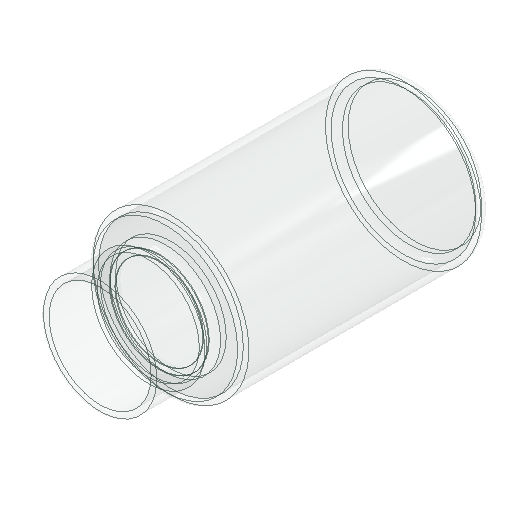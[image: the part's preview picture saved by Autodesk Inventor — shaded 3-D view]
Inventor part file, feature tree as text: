
AUTODESK INVENTOR PART (.ipt)
format: ipt  version: 2024 (Build 280153000, 153)  size: 227,840 bytes
history: native  units: mm
features: fillet x3, revolve x1, shell x1, sketch x1
ambient origin geometry x8: Origin, YZ Plane, XZ Plane, XY Plane, X Axis, Y Axis, Z Axis, Center Point
bodies: Volumenkörper1 (feature_tree)
feature tree (6):
  revolve  "Umdrehung1"
  fillet  "Rundung1"  Radius=13.75mm
  fillet  "Rundung2"  Radius=2.0mm
  shell  "Wandung1"  Thickness=5.0mm
  fillet  "Rundung4"  Radius=56.0mm
  sketch  "Skizze1"  dims[d7=10.0mm d8=90.0deg d9=2.0mm d10=1.0mm d11=1.0mm d13=0.5mm d14=44.0mm]
